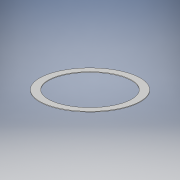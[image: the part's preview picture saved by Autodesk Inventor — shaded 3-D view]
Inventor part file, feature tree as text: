
AUTODESK INVENTOR PART (.ipt)
format: ipt  version: 2018 (Build 220112000, 112)  size: 99,840 bytes
history: native  units: mm
features: extrude x1, sketch x1
ambient origin geometry x8: Origin, YZ Plane, XZ Plane, XY Plane, X Axis, Y Axis, Z Axis, Center Point
bodies: Solid1 (feature_tree)
feature tree (2):
  extrude  "Extrusion1"  Depth=0.2mm
  sketch  "Sketch1"  dims[d0=29.0mm d1=24.0mm d2=0.2mm d3=0.0mm]
